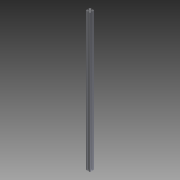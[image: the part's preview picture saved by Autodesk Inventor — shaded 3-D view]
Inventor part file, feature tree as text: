
AUTODESK INVENTOR PART (.ipt)
format: ipt  version: 2016 (Build 200138000, 138)  size: 213,504 bytes
history: native  units: mm
features: other x42, sketch x5, hole x4, extrude x1
ambient origin geometry x8: Origin, YZ Plane, XZ Plane, XY Plane, X Axis, Y Axis, Z Axis, Center Point
bodies: Solid1 (feature_tree)
feature tree (52):
  extrude  "Extrusion1"  [1 undecoded]
  hole  "Drilling 1"  [1 undecoded]
  hole  "Drilling 2"  [1 undecoded]
  hole  "Drilling 3"  [1 undecoded]
  hole  "Drilling 4"  [1 undecoded]
  other  "side_4d_XY"
  other  "side_4d_YZ"
  other  "side_4d_ZX"
  other  "side_4d_X"
  other  "side_4d_Y"
  other  "side_4d_Z"
  other  "side_4d_Center"
  other  "side_1a_XY"
  other  "side_1a_YZ"
  other  "side_1a_ZX"
  other  "side_1a_X"
  other  "side_1a_Y"
  other  "side_1a_Z"
  other  "side_1a_Center"
  other  "side_2b_XY"
  other  "side_2b_YZ"
  other  "side_2b_ZX"
  other  "side_2b_X"
  other  "side_2b_Y"
  other  "side_2b_Z"
  other  "side_2b_Center"
  other  "side_3c_XY"
  other  "side_3c_YZ"
  other  "side_3c_ZX"
  other  "side_3c_X"
  other  "side_3c_Y"
  other  "side_3c_Z"
  other  "side_3c_Center"
  other  "end_XY"
  other  "end_YZ"
  other  "end_ZX"
  other  "end_X"
  other  "end_Y"
  other  "end_Z"
  other  "end_Center"
  other  "start_XY"
  other  "start_YZ"
  other  "start_ZX"
  other  "start_X"
  other  "start_Y"
  other  "start_Z"
  other  "start_Center"
  sketch  "Skizze_1"  dims[d0=1360.0mm d1=0.0mm]
  sketch  "Sketch2"  dims[d2=5.0mm d3=6.0mm d4=4.0mm d5=2.0mm d6=90.0deg d7=6000.0mm d8=0.0mm]
  sketch  "Sketch3"  dims[d9=5.0mm d10=6.0mm d11=4.0mm d12=2.0mm d13=90.0deg d14=6000.0mm d15=0.0mm]
  sketch  "Sketch4"  dims[d16=5.0mm d17=6.0mm d18=4.0mm d19=2.0mm d20=90.0deg d21=6000.0mm d22=0.0mm]
  sketch  "Sketch5"  dims[d23=5.0mm d24=6.0mm d25=4.0mm d26=2.0mm d27=90.0deg d28=6000.0mm d29=0.0mm]
note: 5 required parameter values undecoded (feature->parameter linkage not recoverable at this tier; creation-order binding heuristic only, values carry confidence <= 0.55)
